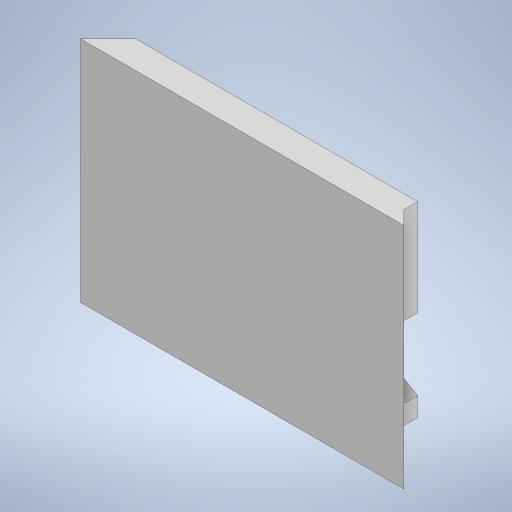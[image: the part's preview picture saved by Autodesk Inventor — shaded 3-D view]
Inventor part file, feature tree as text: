
AUTODESK INVENTOR PART (.ipt)
format: ipt  version: 2023 (Build 270158000, 158)  size: 242,688 bytes
history: native  units: mm
features: reference x4, other x3, extrude x2, sketch x2, plane x1, chamfer x1, draft x1, projected_geometry x1
ambient origin geometry x8: Origin, YZ Plane, XZ Plane, XY Plane, X Axis, Y Axis, Z Axis, Center Point
bodies: Solid1 (feature_tree)
feature tree (15):
  plane  "Work Plane1"
  extrude  "Extrusion1"  Depth=2.0mm TaperAngle=45.0deg
  chamfer  "Chamfer1"  Distance=2.0mm
  draft  "FaceDraft1"
  extrude  "Extrusion2"  [1 undecoded]
  sketch  "Sketch1"  dims[d0=2.0mm d1=0.0mm d2=2.0mm d3=2.0mm d4=45.0deg]
  reference  "Reference1"
  reference  "Reference2"
  reference  "Reference3"
  reference  "Reference4"
  sketch  "Sketch2"  dims[d5=45.0deg d6=2.0mm d7=0.0mm]
  projected_geometry  "Projected Loop1"
  other  "<userpath>\Documents\GitHub\AudMix\3dModels\Assembly.iam"
  other  "Assembly.iam"
  other  "ButtonPanelNew:1"
note: 1 required parameter value undecoded (feature->parameter linkage not recoverable at this tier; creation-order binding heuristic only, values carry confidence <= 0.55)
